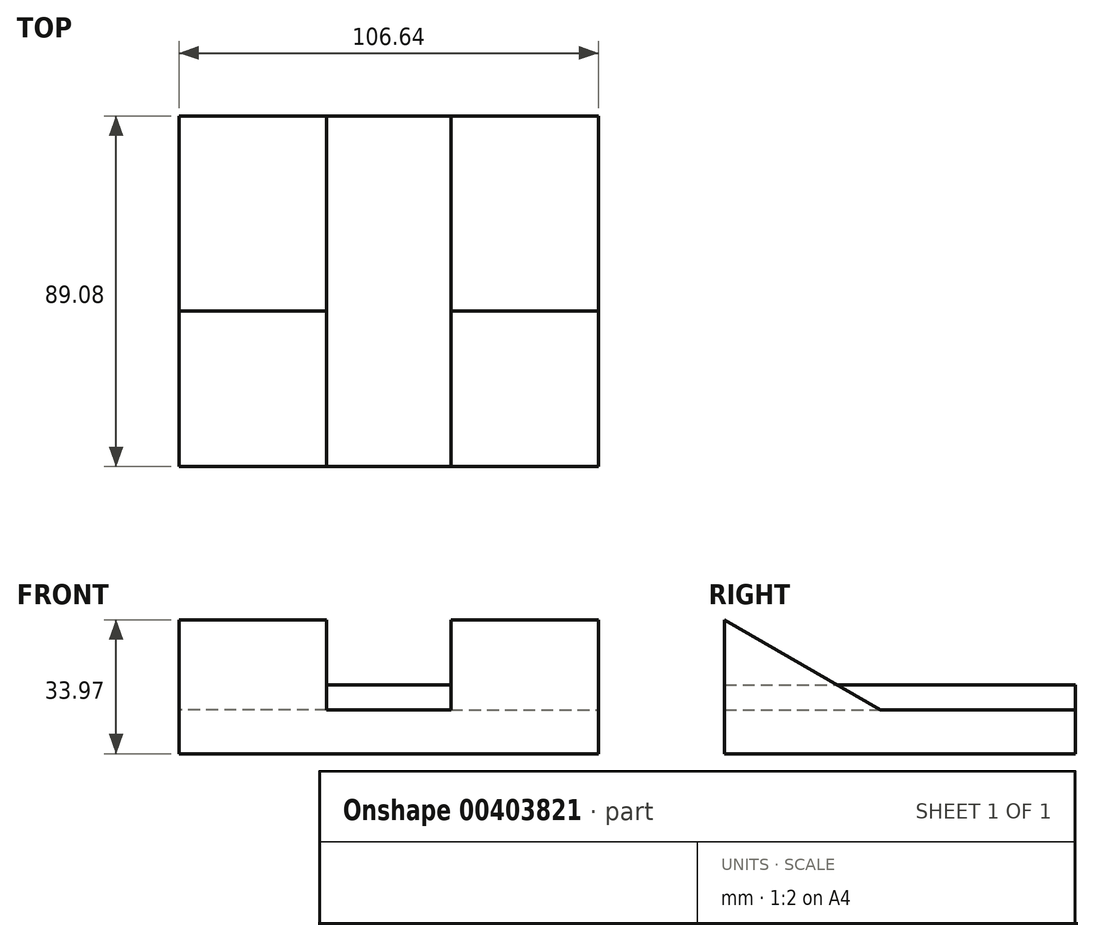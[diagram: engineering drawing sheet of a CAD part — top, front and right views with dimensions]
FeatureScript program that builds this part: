
annotation { "Feature Type Name" : "Feature", "Feature Type Description" : "" }
export const myFeature = defineFeature(function(context is Context, id is Id, definition is map)
    precondition{}
    {
        {
            var Q0;
            Q0=qCreatedBy(makeId("Top.planeOp"),FACE);
            var sketch = newSketch(context, id + "F0", { "sketchPlane" : qUnion([Q0])});
            skLineSegment(sketch, "E0.bottom", {"start": v(53.32, -44.54) * mm, "end": v(-53.32, -44.54) * mm});
            skLineSegment(sketch, "E0.top", {"start": v(53.32, 44.54) * mm, "end": v(-53.32, 44.54) * mm});
            skLineSegment(sketch, "E0.left", {"start": v(53.32, -44.54) * mm, "end": v(53.32, 44.54) * mm});
            skLineSegment(sketch, "E0.right", {"start": v(-53.32, -44.54) * mm, "end": v(-53.32, 44.54) * mm});
            skPoint(sketch, "E0.middle", {"position": v(0, 0) * mm});
            skSolve(sketch);
        }
        {
            var Q0;
            Q0 = qSketchRegion(id + "F0", true);
            extrude(context, id + "F1", {"entities" : qUnion([Q0]), "depth" : 11.14 * mm});
        }
        {
            var Q0;
            Q0=makeQuery(id+"F1.opExtrude","SWEPT_FACE",FACE,{"disambiguationData":[OSD([sQuery(id+"F0.wireOp",EDGE,"E0.right")])]});
            var sketch = newSketch(context, id + "F2", { "sketchPlane" : qUnion([Q0])});
            skLineSegment(sketch, "E1", {"start": v(44.54, 11.14) * mm, "end": v(44.54, 33.97) * mm});
            skLineSegment(sketch, "E2", {"start": v(44.54, 33.97) * mm, "end": v(5.01, 11.14) * mm});
            skLineSegment(sketch, "E3", {"start": v(44.54, 11.14) * mm, "end": v(5.01, 11.14) * mm});
            skSolve(sketch);
        }
        {
            var Q0;
            Q0 = qSketchRegion(id + "F2", true);
            extrude(context, id + "F3", {"entities" : qUnion([Q0]), "oppositeDirection" : true, "depth" : 37.55 * mm});
        }
        {
            var Q0;
            Q0=makeQuery(id+"F3.opExtrude","SWEPT_BODY",BODY,{"disambiguationData":[OSD([sQuery(id+"F2.wireOp",EDGE,"E1"),sQuery(id+"F2.wireOp",EDGE,"E2"),sQuery(id+"F2.wireOp",EDGE,"E3")])]});
            var Q1;
            Q1=qCreatedBy(makeId("Right.planeOp"),FACE);
            mirror(context, id + "F4", {"operationType" : NewBodyOperationType.ADD, "entities" : qUnion([Q0]), "mirrorPlane" : qUnion([Q1])});
        }
        {
            var Q0;
            Q0=makeQuery(id+"F1.opExtrude","CAP_FACE",FACE,{"disambiguationData":[OSD([sQuery(id+"F0.wireOp",EDGE,"E0.bottom"),sQuery(id+"F0.wireOp",EDGE,"E0.top"),sQuery(id+"F0.wireOp",EDGE,"E0.left"),sQuery(id+"F0.wireOp",EDGE,"E0.right")])],"isStart":false});
            var sketch = newSketch(context, id + "F5", { "sketchPlane" : qUnion([Q0])});
            skLineSegment(sketch, "E4.bottom", {"start": v(-15.77, -44.54) * mm, "end": v(15.77, -44.54) * mm});
            skLineSegment(sketch, "E4.top", {"start": v(-15.77, 44.54) * mm, "end": v(15.77, 44.54) * mm});
            skLineSegment(sketch, "E4.left", {"start": v(-15.77, -44.54) * mm, "end": v(-15.77, 44.54) * mm});
            skLineSegment(sketch, "E4.right", {"start": v(15.77, -44.54) * mm, "end": v(15.77, 44.54) * mm});
            skSolve(sketch);
        }
        {
            var Q0;
            {var subQ5=sQuery(id+"F5.wireOp",EDGE,"E4.bottom");Q0=makeQuery(id+"F5.imprint","IMPRINT",FACE,{"disambiguationData":[TD([[makeQuery(id+"F5.imprint","IMPRINT",EDGE,{"derivedFrom":subQ5}),-1.0]])]});}
            extrude(context, id + "F6", {"entities" : qUnion([Q0]), "depth" : 6.37 * mm});
        }
    });
